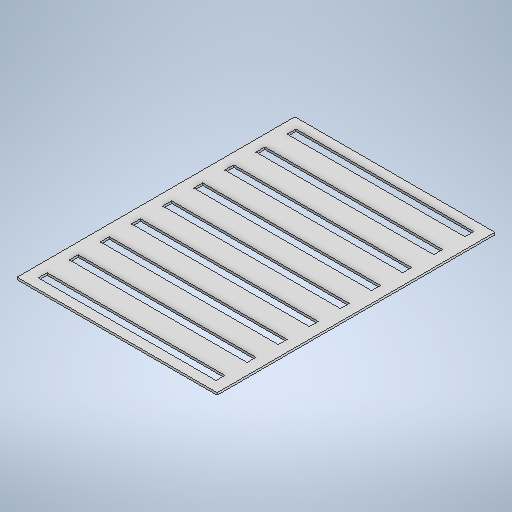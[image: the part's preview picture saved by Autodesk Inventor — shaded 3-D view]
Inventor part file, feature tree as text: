
AUTODESK INVENTOR PART (.ipt)
format: ipt  version: 2025 (Build 290162000, 162)  size: 306,176 bytes
history: native  units: in
note: dims shown in document units (in); Inventor stores cm internally (conversion verified against a paired STEP export)
features: extrude x1, sketch x1
ambient origin geometry x8: Origin, YZ Plane, XZ Plane, XY Plane, X Axis, Y Axis, Z Axis, Center Point
bodies: Solid1 (feature_tree)
feature tree (2):
  extrude  "Extrusion1"  Depth=35.4331in
  sketch  "Sketch1"  dims[d0=49.2126in d1=35.4331in d2=31.4961in d3=1.5748in d7=1.5748in d9=1.5748in d10=1.7717in d11=3.937in d12=3.937in d14=1.5748in d16=1.5748in d18=1.5748in d20=1.5748in d22=1.5748in d24=1.5748in d27=3.937in d28=3.937in d29=3.937in d30=3.937in d31=3.937in d32=3.937in d33=0.3937in d34=0.0in d36=1.9685in]
